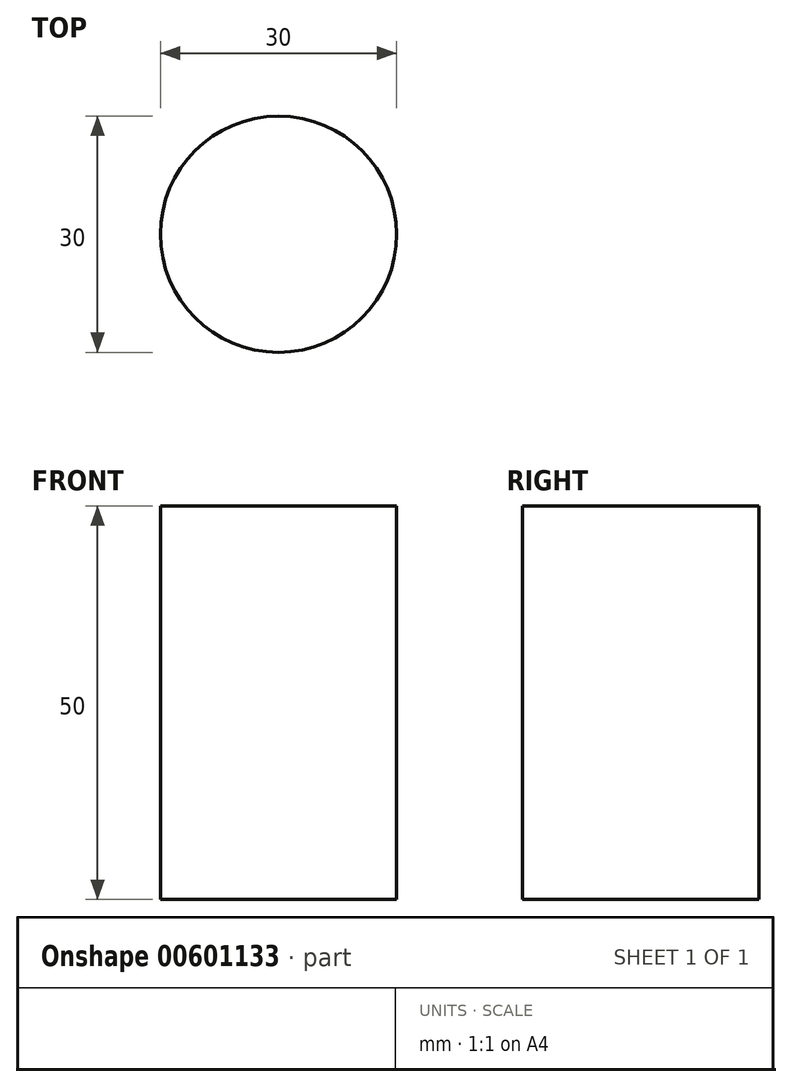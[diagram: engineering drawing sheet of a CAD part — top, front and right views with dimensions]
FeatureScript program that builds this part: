
annotation { "Feature Type Name" : "Feature", "Feature Type Description" : "" }
export const myFeature = defineFeature(function(context is Context, id is Id, definition is map)
    precondition{}
    {
        {
            var Q0;
            Q0=qCreatedBy(makeId("Top.planeOp"),FACE);
            var sketch = newSketch(context, id + "F0", { "sketchPlane" : qUnion([Q0])});
            skCircle(sketch, "E0", {"center": v(0, 0) * mm, "radius": 15 * mm});
            skSolve(sketch);
        }
        {
            var Q0;
            Q0 = qSketchRegion(id + "F0", true);
            extrude(context, id + "F1", {"entities" : qUnion([Q0]), "depth" : 50 * mm, "offsetDistance" : 25 * mm});
        }
    });
